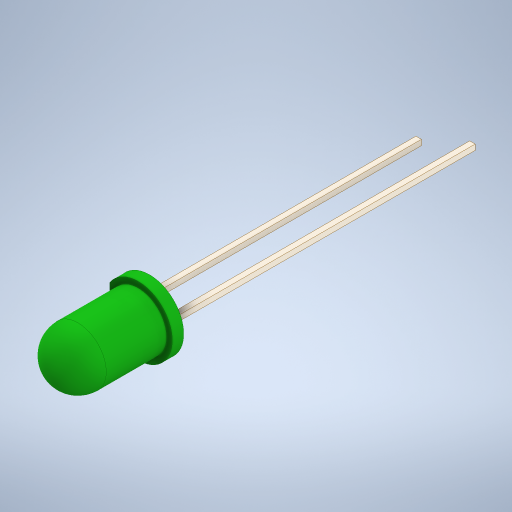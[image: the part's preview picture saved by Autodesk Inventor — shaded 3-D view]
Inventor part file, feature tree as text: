
AUTODESK INVENTOR PART (.ipt)
format: ipt  version: 2023 (Build 270158000, 158)  size: 290,304 bytes
history: imported  units: in
note: dims shown in document units (in); Inventor stores cm internally (conversion verified against a paired STEP export)
features: imported_body x1
ambient origin geometry x8: Origin, YZ Plane, XZ Plane, XY Plane, X Axis, Y Axis, Z Axis, Center Point
bodies: Solid1 (imported_parasolid), Solid2 (imported_parasolid), Solid3 (imported_parasolid), Body1 (imported_parasolid), Body2 (imported_parasolid), Body3 (imported_parasolid)
feature tree (1):
  imported_body  NMx_Import_Brep_tag  [imported B-rep: ~42 faces, bbox_mm=[4.1, 4.158312, 33.3]]
